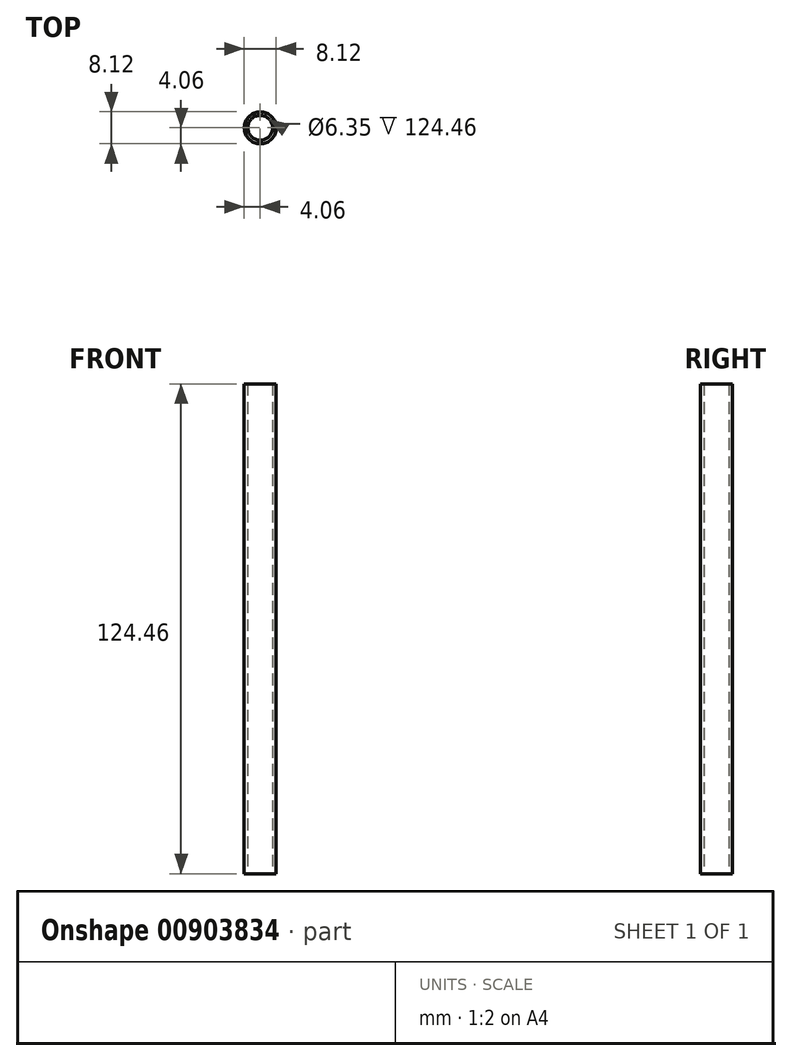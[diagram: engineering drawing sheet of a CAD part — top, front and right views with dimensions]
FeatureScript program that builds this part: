
annotation { "Feature Type Name" : "Feature", "Feature Type Description" : "" }
export const myFeature = defineFeature(function(context is Context, id is Id, definition is map)
    precondition{}
    {
        {
            var Q0;
            Q0=qCreatedBy(makeId("Top.planeOp"),FACE);
            var sketch = newSketch(context, id + "F0", { "sketchPlane" : qUnion([Q0])});
            skCircle(sketch, "E0", {"center": v(0, 0) * mm, "radius": 3.18 * mm});
            skCircle(sketch, "E1", {"center": v(0, 0) * mm, "radius": 4.06 * mm});
            skSolve(sketch);
        }
        {
            var Q0;
            Q0=makeQuery(id+"F0.imprint","IMPRINT",FACE,{"disambiguationData":[TD([[makeQuery(id+"F0.imprint","IMPRINT",EDGE,{"derivedFrom":sQuery(id+"F0.wireOp",EDGE,"E0")}),-1.0]])]});
            extrude(context, id + "F1", {"entities" : qUnion([Q0]), "depth" : 124.46 * mm, "offsetDistance" : 25.4 * mm});
        }
    });
